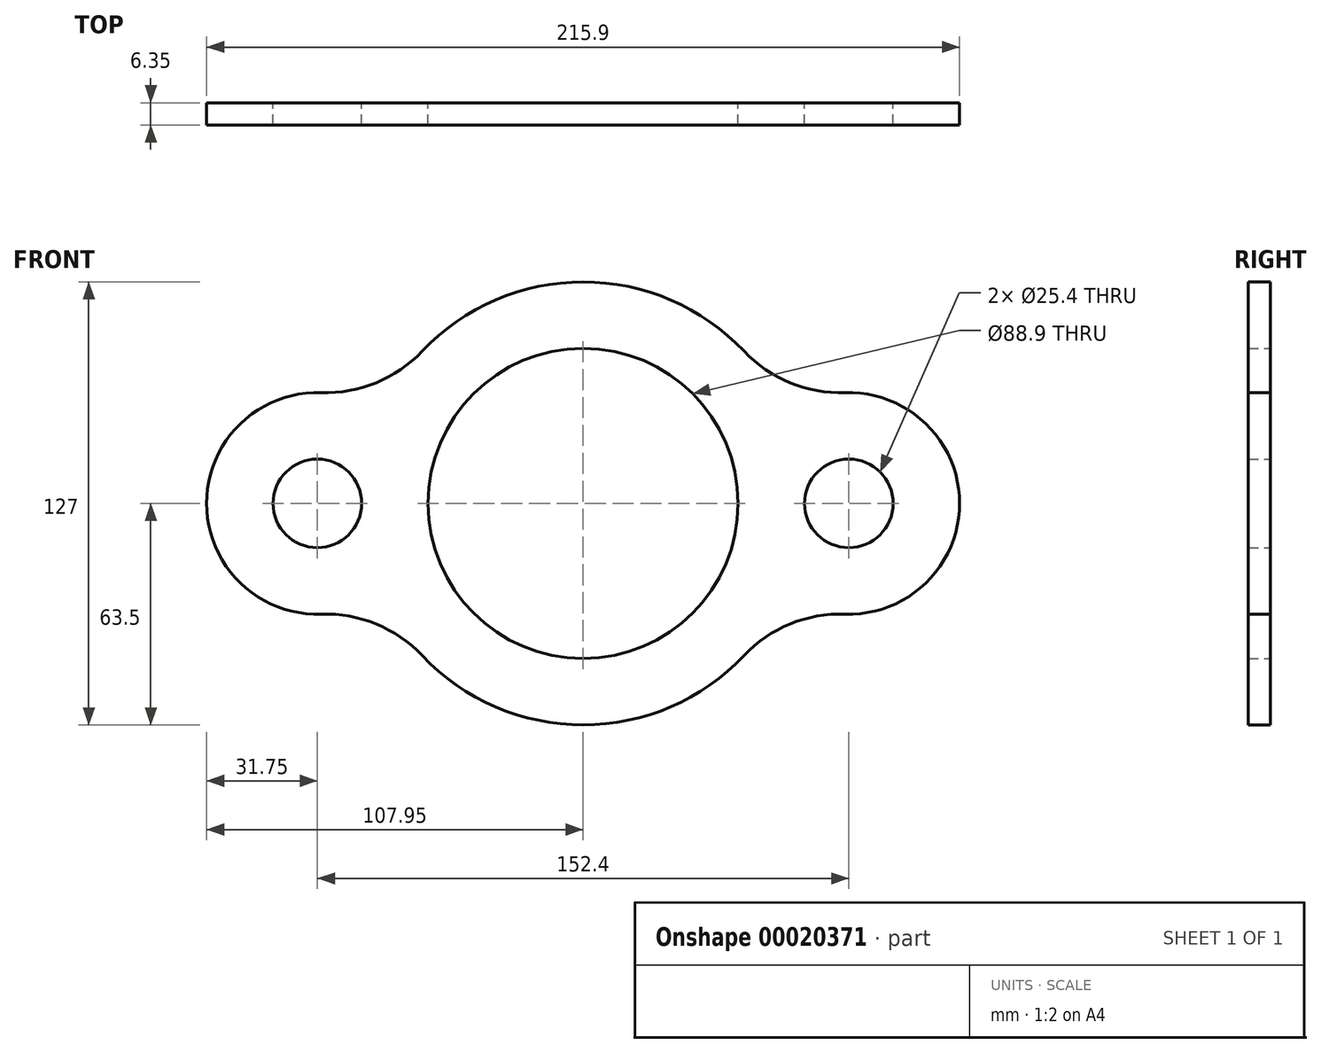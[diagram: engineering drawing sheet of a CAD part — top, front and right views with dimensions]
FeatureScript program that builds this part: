
annotation { "Feature Type Name" : "Feature", "Feature Type Description" : "" }
export const myFeature = defineFeature(function(context is Context, id is Id, definition is map)
    precondition{}
    {
        {
            var Q0;
            Q0=qCreatedBy(makeId("Front.planeOp"),FACE);
            var sketch = newSketch(context, id + "F0", { "sketchPlane" : qUnion([Q0])});
            skCircle(sketch, "E0", {"center": v(0, 0) * mm, "radius": 44.45 * mm});
            skCircle(sketch, "E1", {"center": v(-76.2, 0) * mm, "radius": 12.7 * mm});
            skArc(sketch, "E2", {"start": v(-46.14, -43.63) * mm, "mid": v(0, -63.5) * mm, "end": v(46.14, -43.63) * mm});
            skArc(sketch, "E3", {"start": v(-75.12, 31.73) * mm, "mid": v(-107.95, 0) * mm, "end": v(-75.12, -31.73) * mm});
            skCircle(sketch, "E4", {"center": v(76.2, 0) * mm, "radius": 12.7 * mm});
            skArc(sketch, "E5", {"start": v(75.12, -31.73) * mm, "mid": v(107.95, 0) * mm, "end": v(75.12, 31.73) * mm});
            skArc(sketch, "E6.trimOffspring", {"start": v(46.14, 43.63) * mm, "mid": v(0, 63.5) * mm, "end": v(-46.14, 43.63) * mm});
            skArc(sketch, "E7.filletArc", {"start": v(-75.12, 31.73) * mm, "mid": v(-59.35, 34.56) * mm, "end": v(-46.14, 43.63) * mm});
            skArc(sketch, "E8.filletArc", {"start": v(-46.14, -43.63) * mm, "mid": v(-59.35, -34.56) * mm, "end": v(-75.12, -31.73) * mm});
            skArc(sketch, "E9.filletArc", {"start": v(75.12, -31.73) * mm, "mid": v(59.35, -34.56) * mm, "end": v(46.14, -43.63) * mm});
            skArc(sketch, "E10.filletArc", {"start": v(46.14, 43.63) * mm, "mid": v(59.35, 34.56) * mm, "end": v(75.12, 31.73) * mm});
            skSolve(sketch);
        }
        {
            var Q0;
            Q0=makeQuery(id+"F0.imprint","IMPRINT",FACE,{"disambiguationData":[TD([[makeQuery(id+"F0.imprint","IMPRINT",EDGE,{"derivedFrom":sQuery(id+"F0.wireOp",EDGE,"E0")}),-1.0]])]});
            extrude(context, id + "F1", {"entities" : qUnion([Q0]), "depth" : 6.35 * mm});
        }
    });
